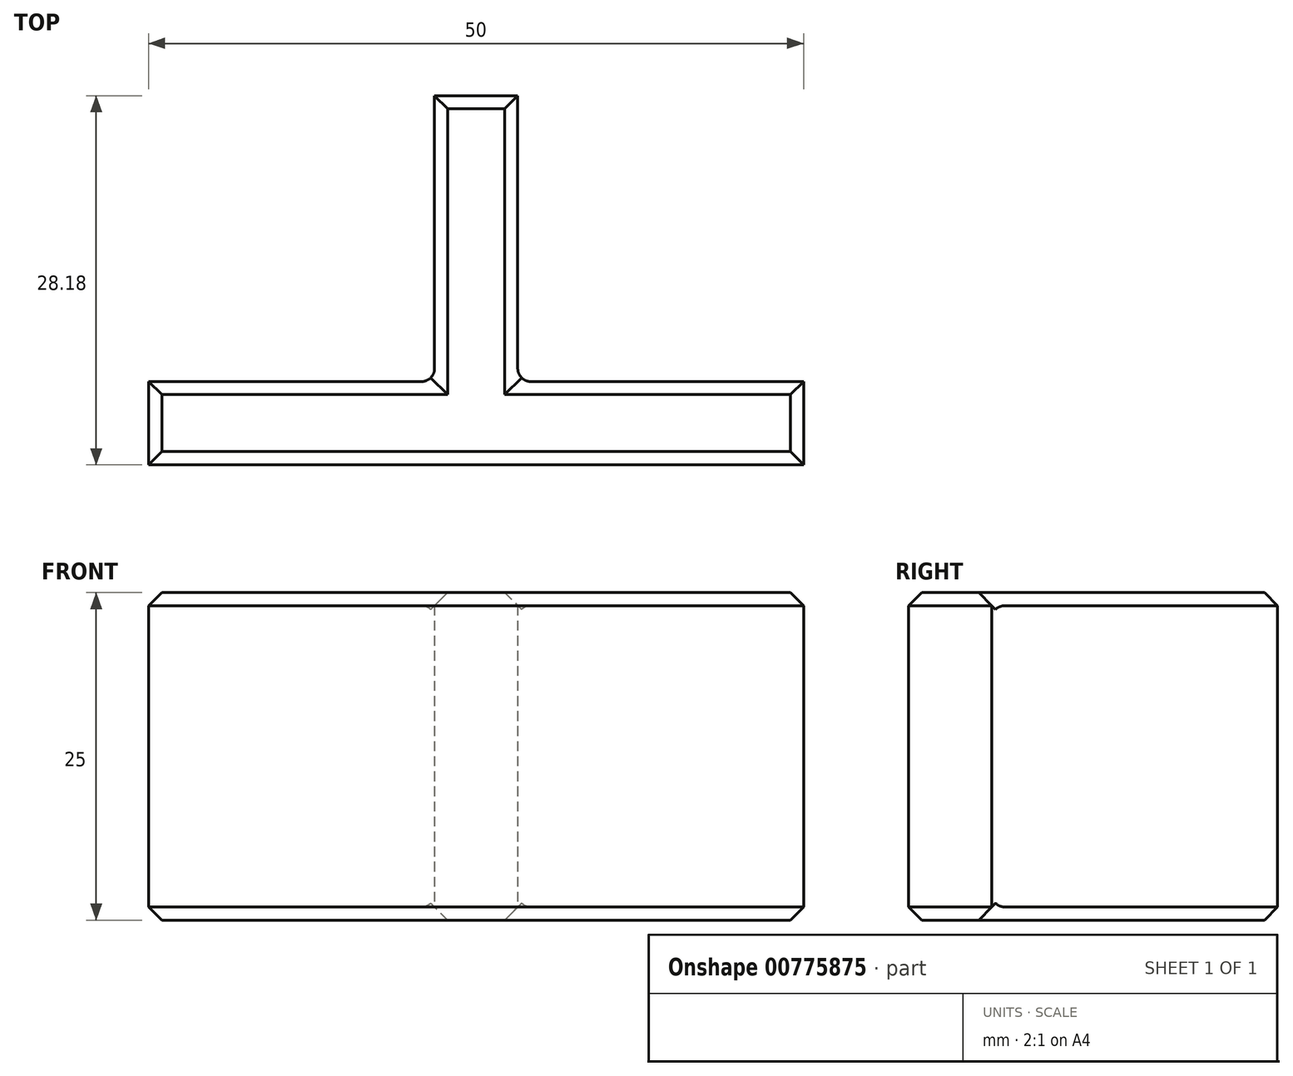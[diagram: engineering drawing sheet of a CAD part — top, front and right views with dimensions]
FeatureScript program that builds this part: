
annotation { "Feature Type Name" : "Feature", "Feature Type Description" : "" }
export const myFeature = defineFeature(function(context is Context, id is Id, definition is map)
    precondition{}
    {
        {
            var Q0;
            Q0=qCreatedBy(makeId("Top.planeOp"),FACE);
            var sketch = newSketch(context, id + "F0", { "sketchPlane" : qUnion([Q0])});
            skLineSegment(sketch, "E0", {"start": v(0, 0) * mm, "end": v(0, 25) * mm, "construction": true});
            skLineSegment(sketch, "E1", {"start": v(25, 0) * mm, "end": v(0, 0) * mm, "construction": true});
            skLineSegment(sketch, "E2", {"start": v(0, 0) * mm, "end": v(0, -25) * mm, "construction": true});
            skLineSegment(sketch, "E3", {"start": v(0, 0) * mm, "end": v(-25, 0) * mm, "construction": true});
            skLineSegment(sketch, "E4.bottom", {"start": v(3.17, 25) * mm, "end": v(-3.17, 25) * mm});
            skLineSegment(sketch, "E4.top", {"start": v(3.17, -25) * mm, "end": v(-3.17, -25) * mm});
            skLineSegment(sketch, "E4.left", {"start": v(3.17, 25) * mm, "end": v(3.17, -25) * mm});
            skLineSegment(sketch, "E4.right", {"start": v(-3.17, 25) * mm, "end": v(-3.17, -25) * mm});
            skPoint(sketch, "E4.middle", {"position": v(0, 0) * mm});
            skLineSegment(sketch, "E5.bottom", {"start": v(-25, 3.17) * mm, "end": v(25, 3.17) * mm});
            skLineSegment(sketch, "E5.top", {"start": v(-25, -3.17) * mm, "end": v(25, -3.17) * mm});
            skLineSegment(sketch, "E5.left", {"start": v(-25, 3.17) * mm, "end": v(-25, -3.17) * mm});
            skLineSegment(sketch, "E5.right", {"start": v(25, 3.17) * mm, "end": v(25, -3.17) * mm});
            skSolve(sketch);
        }
        {
            var Q0;
            {var subQ5=sQuery(id+"F0.wireOp",EDGE,"E5.left");Q0=makeQuery(id+"F0.imprint","IMPRINT",FACE,{"disambiguationData":[TD([[makeQuery(id+"F0.imprint","IMPRINT",EDGE,{"derivedFrom":subQ5}),1.0]])]});}
            var Q1;
            {var subQ0=sQuery(id+"F0.wireOp",EDGE,"E5.bottom");var subQ1=sQuery(id+"F0.wireOp",EDGE,"E4.left");var subQ2=makeQuery(id+"F0.imprint","INTERSECT",VERTEX,{"derivedFrom":[subQ1,subQ0]});Q1=makeQuery(id+"F0.imprint","IMPRINT",FACE,{"disambiguationData":[TD([[makeQuery(id+"F0.imprint","IMPRINT",EDGE,{"disambiguationData":[TD([[subQ2,-1.0]])],"derivedFrom":subQ1}),-1.0]])]});}
            var Q2;
            {var subQ5=sQuery(id+"F0.wireOp",EDGE,"E5.right");Q2=makeQuery(id+"F0.imprint","IMPRINT",FACE,{"disambiguationData":[TD([[makeQuery(id+"F0.imprint","IMPRINT",EDGE,{"derivedFrom":subQ5}),-1.0]])]});}
            var Q3;
            {var subQ0=sQuery(id+"F0.wireOp",EDGE,"E4.bottom");Q3=makeQuery(id+"F0.imprint","IMPRINT",FACE,{"disambiguationData":[TD([[makeQuery(id+"F0.imprint","IMPRINT",EDGE,{"derivedFrom":subQ0}),1.0]])]});}
            extrude(context, id + "F1", {"entities" : qUnion([Q0, Q1, Q2, Q3]), "depth" : 25 * mm, "offsetDistance" : 25 * mm});
        }
        {
            var Q0;
            Q0=makeQuery(id+"F1.opExtrude","CAP_FACE",FACE,{"disambiguationData":[OSD([sQuery(id+"F0.wireOp",EDGE,"E4.bottom"),sQuery(id+"F0.wireOp",EDGE,"E4.left"),sQuery(id+"F0.wireOp",EDGE,"E4.right"),sQuery(id+"F0.wireOp",EDGE,"E5.bottom"),sQuery(id+"F0.wireOp",EDGE,"E5.top"),sQuery(id+"F0.wireOp",EDGE,"E5.left"),sQuery(id+"F0.wireOp",EDGE,"E5.right")])],"isStart":true});
            var Q1;
            Q1=makeQuery(id+"F1.opExtrude","CAP_FACE",FACE,{"disambiguationData":[OSD([sQuery(id+"F0.wireOp",EDGE,"E4.bottom"),sQuery(id+"F0.wireOp",EDGE,"E4.left"),sQuery(id+"F0.wireOp",EDGE,"E4.right"),sQuery(id+"F0.wireOp",EDGE,"E5.bottom"),sQuery(id+"F0.wireOp",EDGE,"E5.top"),sQuery(id+"F0.wireOp",EDGE,"E5.left"),sQuery(id+"F0.wireOp",EDGE,"E5.right")])],"isStart":false});
            chamfer(context, id + "F2", {"entities" : qUnion([Q0, Q1]), "width" : 1 * mm, "tangentPropagation" : true});
        }
        {
            var Q0;
            Q0=makeQuery(id+"F1.opExtrude","SWEPT_EDGE",EDGE,{"disambiguationData":[OSD([sQuery(id+"F0.wireOp",EDGE,"E4.left"),sQuery(id+"F0.wireOp",EDGE,"E5.bottom")])]});
            var Q1;
            Q1=makeQuery(id+"F1.opExtrude","SWEPT_EDGE",EDGE,{"disambiguationData":[OSD([sQuery(id+"F0.wireOp",EDGE,"E4.right"),sQuery(id+"F0.wireOp",EDGE,"E5.bottom")])]});
            fillet(context, id + "F3", {"entities" : qUnion([Q0, Q1]), "radius" : 1 * mm, "tangentPropagation" : true, "allowEdgeOverflow" : false});
        }
    });
